# Revit family: RollHolder-12cm-Vitra-VoyageSeries-A44793
name_source: partatom
category: Plumbing Fixtures
revit_build: Autodesk Revit 2017 (Build: 20160225_1515(x64)
units: mm (PartAtom-declared; Revit-internal decimal feet)

## family parameters
Cut with Voids When Loaded = No
Host = Face
OmniClass Number = 23.45.00.00
OmniClass Title = Sanitary, Laundry, and Cleaning Equipment
Part Type = Normal
Room Calculation Point = No
Round Connector Dimension = Use Diameter
Shared = Yes

## types (4) — shared parameters
BIMobject category = Sanitary - Bathroom Accessories
Brand = VitrA
CW Connection = No
Description = Toilet Roll Holders Voyage Roll Holder
Design country = Turkey
HW Connection = No
IFC Classification = Sanitary Terminal
Main Material = Metal
Manufacturer = Vitra
Manufacturer name = Vitra
Mounting type = Wall Mounted
NBS Referans Code = 35-75-88
NBS Referans Description = Toilet Roll Holders
Nominal Depth (mm) = 150 mm
Nominal Height (mm) = 350 mm  [stored 1.14829 ft]
Nominal Width (mm) = 162 mm
OmniClass Code = 23-31 25 00
OmniClass Description = Toilet and Bath Specialties
Product Type = Built-in Roll Holder
Product certification = https://www.vitraglobal.com
Product data url = https://www.vitraglobal.com
Product family = VoyageSeries
Product group = Roll Holder
Secondary Material = Matte Black
Technical description = https://www.vitraglobal.com
URL = https://vitraglobal.com
Uniclass 1.4 Code = L7313
Uniclass 1.4 Description = Sanitary above ground pipes and fittings
Uniclass 2.0 Code = PR-35-75-88
Uniclass 2.0 Description = Toilet Roll Holders
Uniclass 2015 Code = Pr_40_20_76_88
Uniclass 2015 Name = Toilet roll holders
Uniformat II Description = FURNISHINGS
Vent Connection = No
Warranty Period (Year) = 5 years
Waste Connection = No
Weight Net (kg) = 3.5
Youtube = https://www.youtube.com
zero-valued in all types: Default Elevation

## per-type parameters (varying)
| type | Article No. (default) | Coating Material | Color | Model | Primary Material | Product SKU |
| RollHolder-Vitra-VoyageSeries(Black)-A4479336 | A4479336 | Matte Black | Black | A4479336 | Matte Black | A4479336 |
| RollHolder-Vitra-VoyageSeries(Copper)-A4479355 | A4479355 | Taupe | Copper | A4479355 | BrightCopper | A4479355 |
| RollHolder-Vitra-VoyageSeries(Black)-A4479354 | A4479354 | Taupe | Black | A4479354 | Matte Black | A4479354 |
| RollHolder-Vitra-VoyageSeries(Chrome)-A4479357 | A4479357 | White | Chrome | A4479357 | Chrome | A4479357 |

note: [stored X ft] marks values corroborated as IEEE doubles in the binary element streams (Revit-internal decimal feet)

## geometry (parser evidence)
native form markers: Sweep x3
no freeform markers — native parametric forms only
